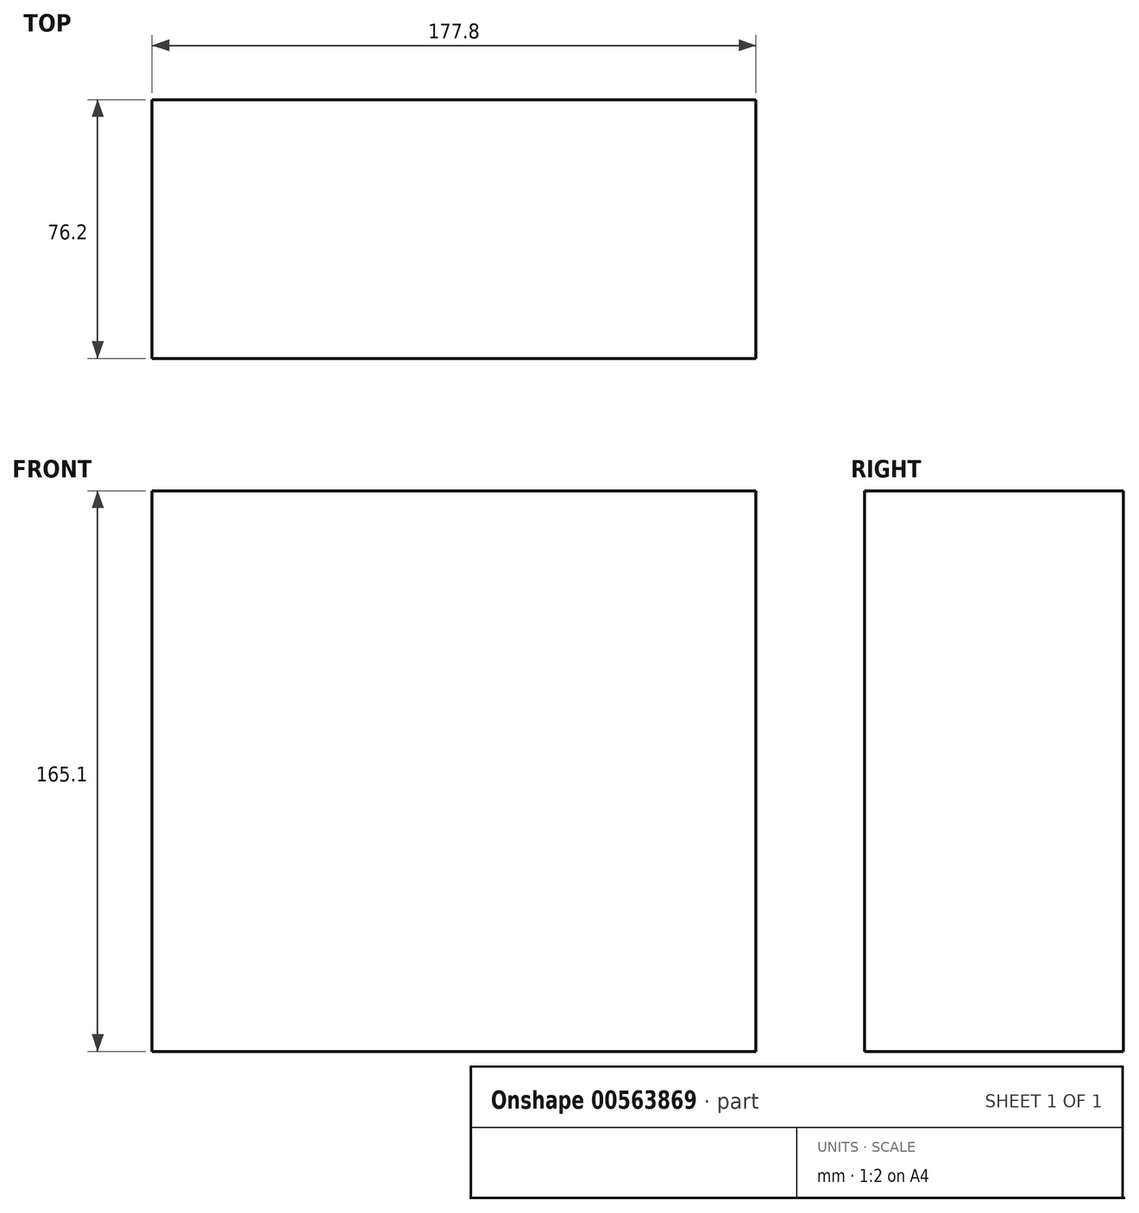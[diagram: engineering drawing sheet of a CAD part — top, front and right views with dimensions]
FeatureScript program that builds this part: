
annotation { "Feature Type Name" : "Feature", "Feature Type Description" : "" }
export const myFeature = defineFeature(function(context is Context, id is Id, definition is map)
    precondition{}
    {
        {
            var Q0;
            Q0=qCreatedBy(makeId("Top.planeOp"),FACE);
            var sketch = newSketch(context, id + "F0", { "sketchPlane" : qUnion([Q0])});
            skLineSegment(sketch, "E0.bottom", {"start": v(0, 0) * mm, "end": v(177.8, 0) * mm});
            skLineSegment(sketch, "E0.top", {"start": v(0, 76.2) * mm, "end": v(177.8, 76.2) * mm});
            skLineSegment(sketch, "E0.left", {"start": v(0, 0) * mm, "end": v(0, 76.2) * mm});
            skLineSegment(sketch, "E0.right", {"start": v(177.8, 0) * mm, "end": v(177.8, 76.2) * mm});
            skSolve(sketch);
        }
        {
            var Q0;
            Q0=makeQuery(id+"F0.imprint","IMPRINT",FACE,{"disambiguationData":[TD([[makeQuery(id+"F0.imprint","IMPRINT",EDGE,{"derivedFrom":sQuery(id+"F0.wireOp",EDGE,"E0.bottom")}),1.0]])]});
            extrude(context, id + "F1", {"entities" : qUnion([Q0]), "depth" : 165.1 * mm, "offsetDistance" : 25.4 * mm});
        }
    });
